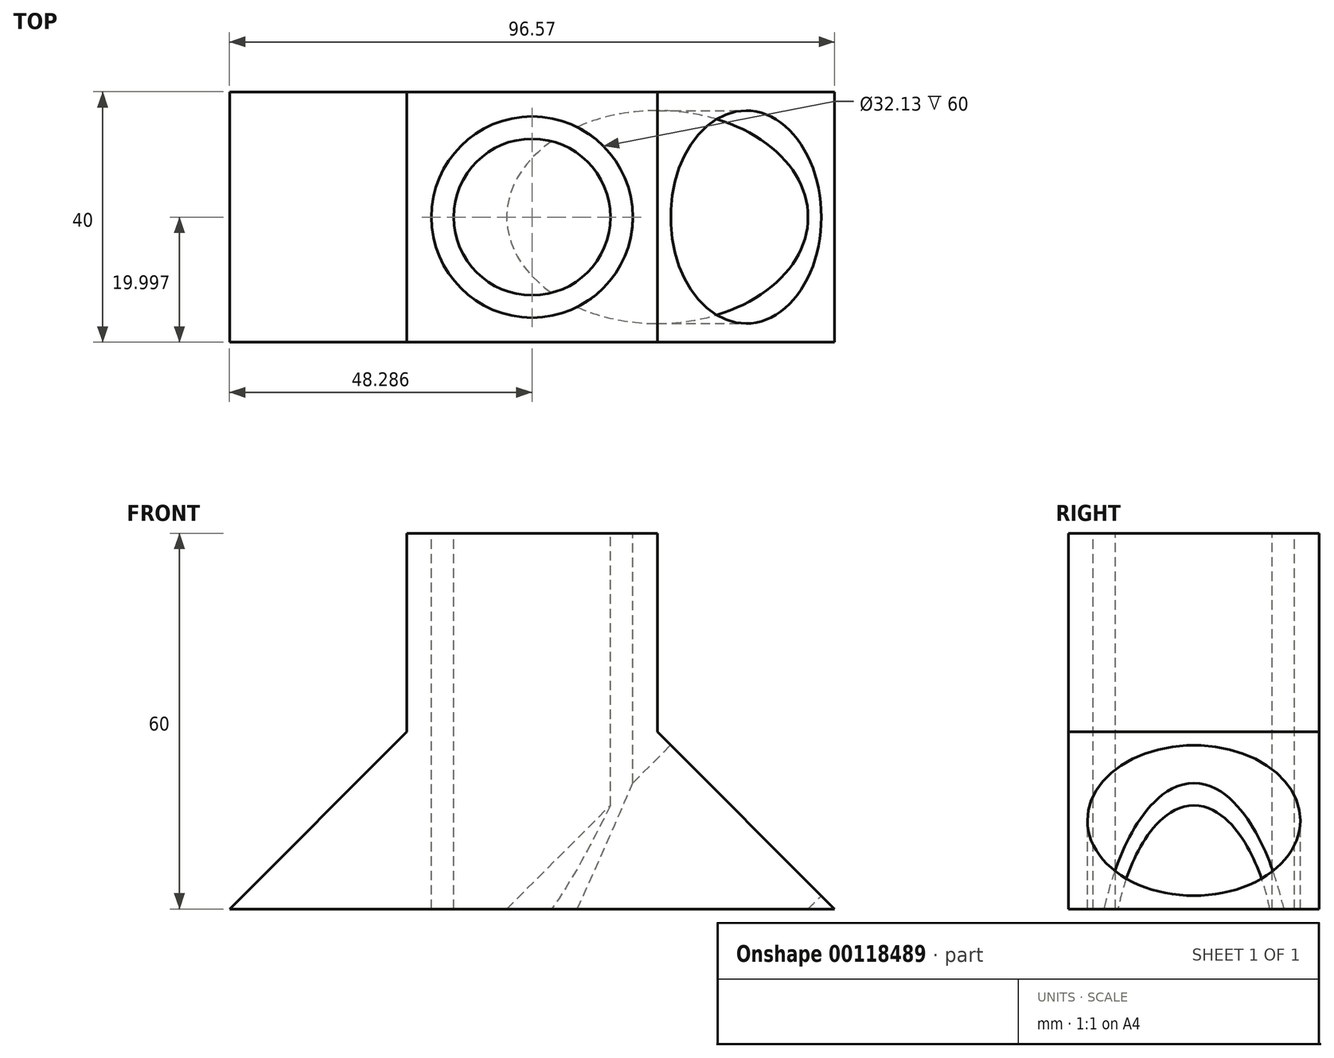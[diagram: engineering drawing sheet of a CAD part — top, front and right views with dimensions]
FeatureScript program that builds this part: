
annotation { "Feature Type Name" : "Feature", "Feature Type Description" : "" }
export const myFeature = defineFeature(function(context is Context, id is Id, definition is map)
    precondition{}
    {
        {
            var Q0;
            Q0=qCreatedBy(makeId("Top.planeOp"),FACE);
            var sketch = newSketch(context, id + "F0", { "sketchPlane" : qUnion([Q0])});
            skLineSegment(sketch, "E0.bottom", {"start": v(-21.7, 47.27) * mm, "end": v(18.3, 47.27) * mm});
            skLineSegment(sketch, "E0.top", {"start": v(-21.7, 7.27) * mm, "end": v(18.3, 7.27) * mm});
            skLineSegment(sketch, "E0.left", {"start": v(-21.7, 47.27) * mm, "end": v(-21.7, 7.27) * mm});
            skLineSegment(sketch, "E0.right", {"start": v(18.3, 47.27) * mm, "end": v(18.3, 7.27) * mm});
            skSolve(sketch);
        }
        {
            var Q0;
            Q0=makeQuery(id+"F0.imprint","IMPRINT",FACE,{"disambiguationData":[TD([[makeQuery(id+"F0.imprint","IMPRINT",EDGE,{"derivedFrom":sQuery(id+"F0.wireOp",EDGE,"E0.bottom")}),-1.0]])]});
            extrude(context, id + "F1", {"entities" : qUnion([Q0]), "depth" : 60 * mm});
        }
        {
            var Q0;
            Q0=makeQuery(id+"F1.opExtrude","SWEPT_FACE",FACE,{"disambiguationData":[OSD([sQuery(id+"F0.wireOp",EDGE,"E0.right")])]});
            var sketch = newSketch(context, id + "F2", { "sketchPlane" : qUnion([Q0])});
            skLineSegment(sketch, "E1.bottom", {"start": v(7.27, 0) * mm, "end": v(47.27, 0) * mm});
            skLineSegment(sketch, "E1.top", {"start": v(7.27, 28.28) * mm, "end": v(47.27, 28.28) * mm});
            skLineSegment(sketch, "E1.left", {"start": v(7.27, 0) * mm, "end": v(7.27, 28.28) * mm});
            skLineSegment(sketch, "E1.right", {"start": v(47.27, 0) * mm, "end": v(47.27, 28.28) * mm});
            skSolve(sketch);
        }
        {
            var Q0;
            Q0=makeQuery(id+"F2.imprint","IMPRINT",FACE,{"disambiguationData":[TD([[makeQuery(id+"F2.imprint","IMPRINT",EDGE,{"derivedFrom":sQuery(id+"F2.wireOp",EDGE,"E1.bottom")}),-1.0]])]});
            extrude(context, id + "F3", {"entities" : qUnion([Q0]), "operationType" : NewBodyOperationType.ADD, "depth" : 28.28 * mm});
        }
        {
            var Q0;
            Q0=makeQuery(id+"F1.opExtrude","SWEPT_FACE",FACE,{"disambiguationData":[OSD([sQuery(id+"F0.wireOp",EDGE,"E0.left")])]});
            var sketch = newSketch(context, id + "F4", { "sketchPlane" : qUnion([Q0])});
            skLineSegment(sketch, "E2.bottom", {"start": v(-7.27, 0) * mm, "end": v(-47.27, 0) * mm});
            skLineSegment(sketch, "E2.top", {"start": v(-7.27, 28.28) * mm, "end": v(-47.27, 28.28) * mm});
            skLineSegment(sketch, "E2.left", {"start": v(-7.27, 0) * mm, "end": v(-7.27, 28.28) * mm});
            skLineSegment(sketch, "E2.right", {"start": v(-47.27, 0) * mm, "end": v(-47.27, 28.28) * mm});
            skSolve(sketch);
        }
        {
            var Q0;
            Q0=makeQuery(id+"F4.imprint","IMPRINT",FACE,{"disambiguationData":[TD([[makeQuery(id+"F4.imprint","IMPRINT",EDGE,{"derivedFrom":sQuery(id+"F4.wireOp",EDGE,"E2.bottom")}),1.0]])]});
            extrude(context, id + "F5", {"entities" : qUnion([Q0]), "operationType" : NewBodyOperationType.ADD, "depth" : 28.28 * mm});
        }
        {
            var Q0;
            Q0=makeQuery(id+"F5.boolean.opBoolean","MERGE",FACE,{"derivedFrom":[makeQuery(id+"F3.boolean.opBoolean","MERGE",FACE,{"derivedFrom":[makeQuery(id+"F1.opExtrude","SWEPT_FACE",FACE,{"disambiguationData":[OSD([sQuery(id+"F0.wireOp",EDGE,"E0.top")])]}),makeQuery(id+"F3.opExtrude","SWEPT_FACE",FACE,{"disambiguationData":[OSD([sQuery(id+"F2.wireOp",EDGE,"E1.left")])]})]}),makeQuery(id+"F5.opExtrude","SWEPT_FACE",FACE,{"disambiguationData":[OSD([sQuery(id+"F4.wireOp",EDGE,"E2.left")])]})]});
            var sketch = newSketch(context, id + "F6", { "sketchPlane" : qUnion([Q0])});
            skLineSegment(sketch, "E3", {"start": v(-21.7, 28.28) * mm, "end": v(-49.98, 0) * mm});
            skLineSegment(sketch, "E4", {"start": v(-49.98, 0) * mm, "end": v(-49.98, 28.28) * mm});
            skLineSegment(sketch, "E5", {"start": v(-49.98, 28.28) * mm, "end": v(-21.7, 28.28) * mm});
            skLineSegment(sketch, "E6", {"start": v(18.3, 28.28) * mm, "end": v(46.6, 28.28) * mm});
            skLineSegment(sketch, "E7", {"start": v(46.6, 28.28) * mm, "end": v(46.6, 0) * mm});
            skLineSegment(sketch, "E8", {"start": v(46.6, 0) * mm, "end": v(18.3, 28.28) * mm});
            skSolve(sketch);
        }
        {
            var Q0;
            Q0=makeQuery(id+"F6.imprint","IMPRINT",FACE,{"disambiguationData":[TD([[makeQuery(id+"F6.imprint","IMPRINT",EDGE,{"derivedFrom":sQuery(id+"F6.wireOp",EDGE,"E3")}),-1.0]])]});
            var Q1;
            Q1=makeQuery(id+"F6.imprint","IMPRINT",FACE,{"disambiguationData":[TD([[makeQuery(id+"F6.imprint","IMPRINT",EDGE,{"derivedFrom":sQuery(id+"F6.wireOp",EDGE,"E6")}),1.0]])]});
            extrude(context, id + "F7", {"entities" : qUnion([Q0, Q1]), "operationType" : NewBodyOperationType.REMOVE, "endBound" : BoundingType.THROUGH_ALL, "oppositeDirection" : true, "depth" : 25 * mm});
        }
        {
            var Q0;
            Q0=makeQuery(id+"F1.opExtrude","CAP_FACE",FACE,{"disambiguationData":[OSD([sQuery(id+"F0.wireOp",EDGE,"E0.bottom"),sQuery(id+"F0.wireOp",EDGE,"E0.top"),sQuery(id+"F0.wireOp",EDGE,"E0.left"),sQuery(id+"F0.wireOp",EDGE,"E0.right")])],"isStart":false});
            var sketch = newSketch(context, id + "F8", { "sketchPlane" : qUnion([Q0])});
            skCircle(sketch, "E9", {"center": v(-1.7, 27.27) * mm, "radius": 12.5 * mm});
            skLineSegment(sketch, "E10", {"start": v(-1.7, 47.27) * mm, "end": v(-1.7, 7.27) * mm, "construction": true});
            skCircle(sketch, "E11", {"center": v(-1.7, 27.27) * mm, "radius": 16.07 * mm});
            skSolve(sketch);
        }
        {
            var Q0;
            Q0=makeQuery(id+"F8.imprint","IMPRINT",FACE,{"disambiguationData":[TD([[makeQuery(id+"F8.imprint","IMPRINT",EDGE,{"derivedFrom":sQuery(id+"F8.wireOp",EDGE,"E9")}),-1.0]])]});
            extrude(context, id + "F9", {"entities" : qUnion([Q0]), "operationType" : NewBodyOperationType.REMOVE, "endBound" : BoundingType.THROUGH_ALL, "oppositeDirection" : true, "depth" : 60 * mm});
        }
        {
            var Q0;
            Q0=makeQuery(id+"F7.boolean.opBoolean","COPY",FACE,{"derivedFrom":makeQuery(id+"F7.opExtrude","SWEPT_FACE",FACE,{"disambiguationData":[OSD([sQuery(id+"F6.wireOp",EDGE,"E8")])]})});
            var sketch = newSketch(context, id + "F10", { "sketchPlane" : qUnion([Q0])});
            skCircle(sketch, "E12", {"center": v(27.27, -12.94) * mm, "radius": 17 * mm});
            skLineSegment(sketch, "E13", {"start": v(27.27, 7.06) * mm, "end": v(27.27, -32.94) * mm, "construction": true});
            skSolve(sketch);
        }
        {
            var Q0;
            Q0=makeQuery(id+"F10.imprint","IMPRINT",FACE,{"disambiguationData":[TD([[makeQuery(id+"F10.imprint","IMPRINT",EDGE,{"derivedFrom":sQuery(id+"F10.wireOp",EDGE,"E12")}),1.0]])]});
            extrude(context, id + "F11", {"entities" : qUnion([Q0]), "operationType" : NewBodyOperationType.REMOVE, "endBound" : BoundingType.THROUGH_ALL, "oppositeDirection" : true, "depth" : 25 * mm});
        }
    });
